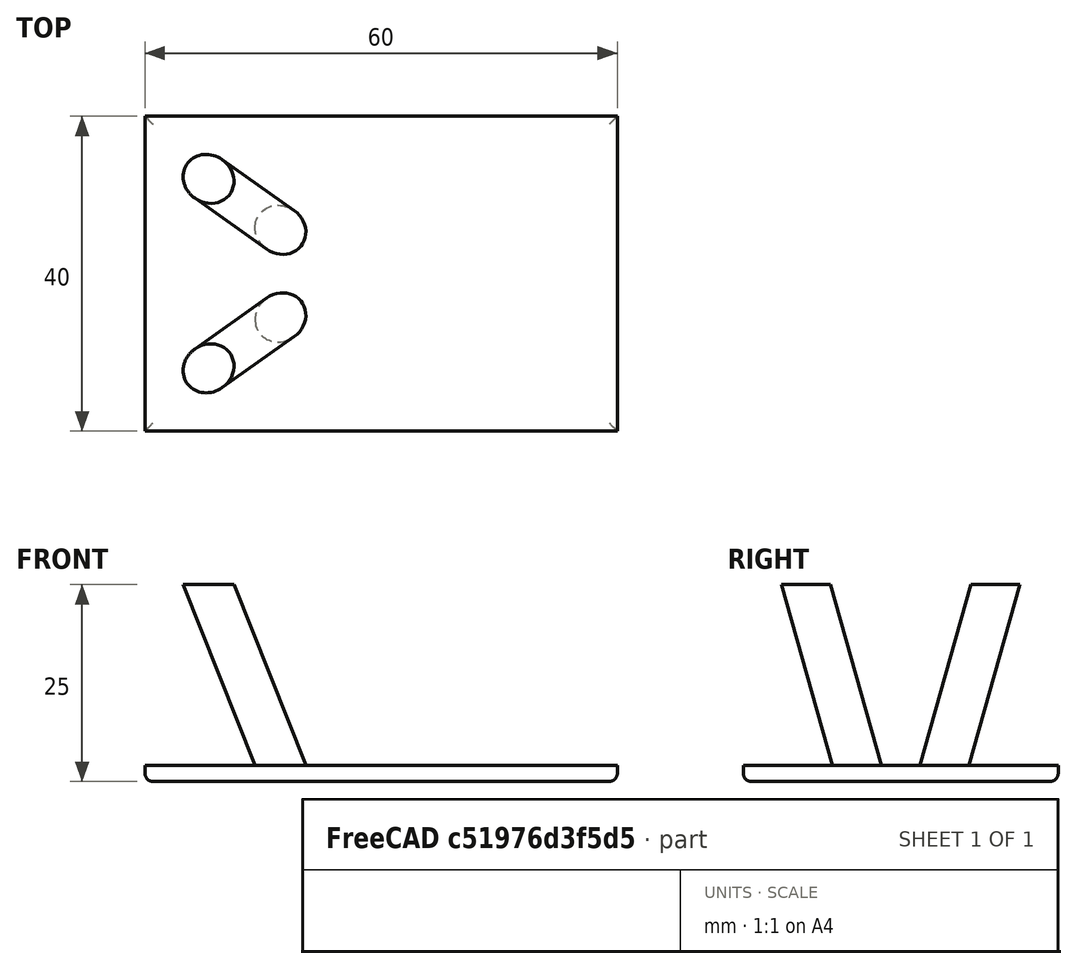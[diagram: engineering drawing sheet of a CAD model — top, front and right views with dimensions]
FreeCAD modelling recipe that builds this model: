
FCSTD DOCUMENT  (FreeCAD 0.14R2935 (Git))
Label: changing-table-1
License: CC-BY 3.0
LicenseURL: http://creativecommons.org/licenses/by/3.0/
objects: Part::Box×3, Part::Mirroring×3, Part::Cut×2, Part::Cylinder×1, Part::Fillet×1
note: 10 computed .brp shape members not serialized (recipe doc carries the construction recipe); baked Part::Feature solids carry a one-line shape summary decoded from their .brp

FEATURE [Part::Box] Box  label="Bordplade"
  Height = 2
  Length = 60
  Placement = pos=(-30,-20,0) rot=(0,0,1;0rad)
  Width = 40
FEATURE [Part::Cylinder] Cylinder  label="Ben 1"
  Angle = 360
  Height = 30
  Placement = pos=(12,5,0) rot=(-0.572298,0.819538,0.02886;0.45295rad)
  Radius = 3
FEATURE [Part::Box] Box001  label="Gulc-cutter"
  Height = 4
  Length = 60
  Placement = pos=(-30,-20,25) rot=(0,0,1;0rad)
  Width = 40
FEATURE [Part::Cut] Cut
  Base = -> Cylinder
  Tool = -> Box001
FEATURE [Part::Box] Box002  label="Bordplade-cutter"
  Height = 6
  Length = 60
  Placement = pos=(-30,-20,-4) rot=(0,0,1;0rad)
  Width = 40
FEATURE [Part::Cut] Cut001  label="ben1-cuttet-final"
  Base = -> Cut
  Tool = -> Box002
FEATURE [Part::Mirroring] Part__Mirroring  label="ben1-cuttet-final (Mirror #1)"
  Base = (0,0,0)
  Normal = (0,1,0)
  Source = -> Cut001
FEATURE [Part::Mirroring] Part__Mirroring001  label="ben1-cuttet-final (Mirror #2)"
  Base = (0,0,0)
  Normal = (1,0,0)
  Source = -> Cut001
FEATURE [Part::Mirroring] Part__Mirroring002  label="ben1-cuttet-final (Mirror #3)"
  Base = (0,0,0)
  Normal = (1,0,0)
  Source = -> Part__Mirroring
FEATURE [Part::Fillet] Fillet
  Base = -> Box
  Edges = 4 edges r=1: [Edge4,Edge8,Edge9,Edge11]
